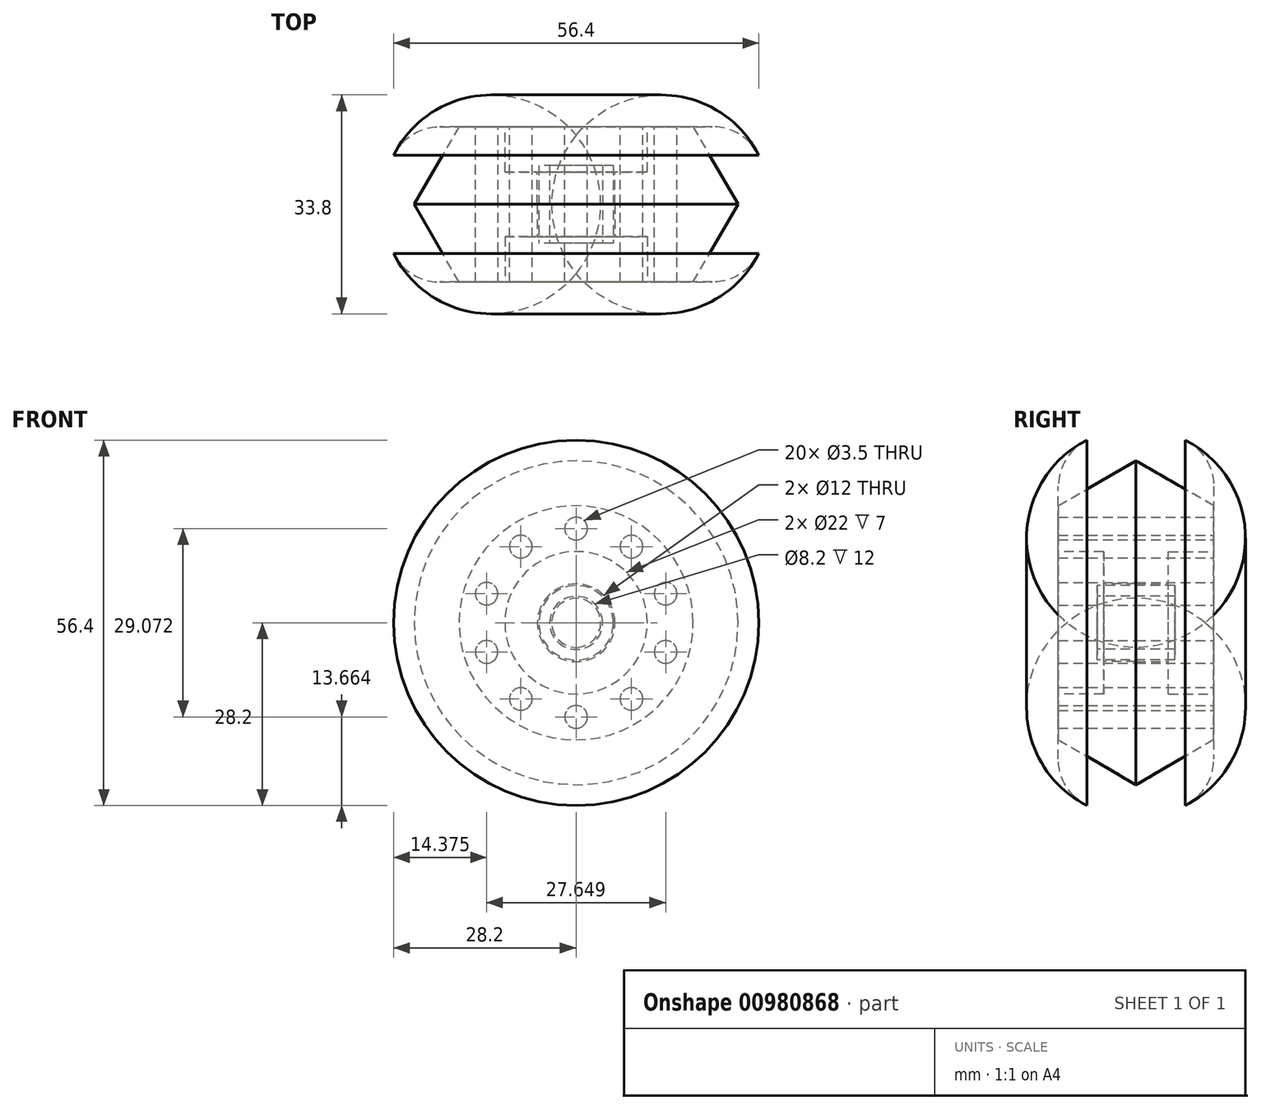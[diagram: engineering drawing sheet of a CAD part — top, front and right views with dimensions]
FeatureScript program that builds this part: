
annotation { "Feature Type Name" : "Feature", "Feature Type Description" : "" }
export const myFeature = defineFeature(function(context is Context, id is Id, definition is map)
    precondition{}
    {
        {
            var Q0;
            Q0=qCreatedBy(makeId("Front.planeOp"),FACE);
            var sketch = newSketch(context, id + "F0", { "sketchPlane" : qUnion([Q0])});
            skCircle(sketch, "E0", {"center": v(0, 0) * mm, "radius": 11 * mm});
            skCircle(sketch, "E1", {"center": v(0, 0) * mm, "radius": 25 * mm});
            skCircle(sketch, "E2", {"center": v(0, 0) * mm, "radius": 6 * mm});
            skCircle(sketch, "E3", {"center": v(0, 0) * mm, "radius": 30 * mm});
            skSolve(sketch);
        }
        {
            var Q0;
            Q0=makeQuery(id+"F0.imprint","IMPRINT",FACE,{"disambiguationData":[TD([[makeQuery(id+"F0.imprint","IMPRINT",EDGE,{"derivedFrom":sQuery(id+"F0.wireOp",EDGE,"E0")}),-1.0]])]});
            var Q1;
            Q1=makeQuery(id+"F0.imprint","IMPRINT",FACE,{"disambiguationData":[TD([[makeQuery(id+"F0.imprint","IMPRINT",EDGE,{"derivedFrom":sQuery(id+"F0.wireOp",EDGE,"E0")}),1.0]])]});
            extrude(context, id + "F1", {"entities" : qUnion([Q0, Q1]), "depth" : 12 * mm, "offsetDistance" : 25 * mm});
        }
        {
            var Q0;
            Q0=makeQuery(id+"F0.imprint","IMPRINT",FACE,{"disambiguationData":[TD([[makeQuery(id+"F0.imprint","IMPRINT",EDGE,{"derivedFrom":sQuery(id+"F0.wireOp",EDGE,"E0")}),1.0]])]});
            extrude(context, id + "F2", {"entities" : qUnion([Q0]), "operationType" : NewBodyOperationType.REMOVE, "depth" : 7 * mm, "offsetDistance" : 25 * mm});
        }
        {
            var Q0;
            Q0=makeQuery(id+"F1.opExtrude","CAP_FACE",FACE,{"disambiguationData":[OSD([sQuery(id+"F0.wireOp",EDGE,"E1"),sQuery(id+"F0.wireOp",EDGE,"E2")])],"isStart":false});
            var sketch = newSketch(context, id + "F3", { "sketchPlane" : qUnion([Q0])});
            skCircle(sketch, "E4", {"center": v(18, 0) * mm, "radius": 2.93 * mm});
            skCircle(sketch, "E5.0", {"center": v(0, 0) * mm, "radius": 11 * mm, "construction": true});
            skCircle(sketch, "E6.0", {"center": v(0, 0) * mm, "radius": 25 * mm, "construction": true});
            skLineSegment(sketch, "E7", {"start": v(11, 0) * mm, "end": v(25, 0) * mm, "construction": true});
            skCircle(sketch, "E8.1.0", {"center": v(0, 18) * mm, "radius": 2.93 * mm});
            skCircle(sketch, "E8.2.0", {"center": v(-18, 0) * mm, "radius": 2.93 * mm});
            skCircle(sketch, "E8.3.0", {"center": v(0, -18) * mm, "radius": 2.93 * mm});
            skLineSegment(sketch, "E9", {"start": v(0, 0) * mm, "end": v(7.78, 7.78) * mm, "construction": true});
            skLineSegment(sketch, "E10", {"start": v(7.78, 7.78) * mm, "end": v(17.68, 17.68) * mm, "construction": true});
            skCircle(sketch, "E11", {"center": v(12.73, 12.73) * mm, "radius": 3.08 * mm});
            skCircle(sketch, "E12.1.0", {"center": v(-12.73, 12.73) * mm, "radius": 3.08 * mm});
            skCircle(sketch, "E12.2.0", {"center": v(-12.73, -12.73) * mm, "radius": 3.08 * mm});
            skCircle(sketch, "E12.3.0", {"center": v(12.73, -12.73) * mm, "radius": 3.08 * mm});
            skSolve(sketch);
        }
        {
            var Q0;
            Q0=qCreatedBy(makeId("Top.planeOp"),FACE);
            var sketch = newSketch(context, id + "F4", { "sketchPlane" : qUnion([Q0])});
            skLineSegment(sketch, "E13", {"start": v(0, 33.2) * mm, "end": v(0, -52.48) * mm, "construction": true});
            skSolve(sketch);
        }
        {
            var Q0;
            Q0=makeQuery(id+"F1.opExtrude","CAP_FACE",FACE,{"disambiguationData":[OSD([sQuery(id+"F0.wireOp",EDGE,"E1"),sQuery(id+"F0.wireOp",EDGE,"E2")])],"isStart":false});
            var sketch = newSketch(context, id + "F5", { "sketchPlane" : qUnion([Q0])});
            skLineSegment(sketch, "E14", {"start": v(-27.1, 0) * mm, "end": v(30.64, 0) * mm});
            skSolve(sketch);
        }
        {
            var Q0;
            Q0=makeQuery(id+"F1.opExtrude","SWEPT_BODY",BODY,{"disambiguationData":[OSD([sQuery(id+"F0.wireOp",EDGE,"E1"),sQuery(id+"F0.wireOp",EDGE,"E2")])]});
            var Q1;
            Q1=sQuery(id+"F5.wireOp",EDGE,"E14");
            transform(context, id + "F6", {"entities" : qUnion([Q0]), "transformType" : TransformType.ROTATION, "transformAxis" : qUnion([Q1]), "angle" : 180 * degree, "makeCopy" : true});
        }
        {
            var Q0;
            Q0=makeQuery(id+"F6.opPattern","COPY",BODY,{"derivedFrom":makeQuery(id+"F1.opExtrude","SWEPT_BODY",BODY,{"disambiguationData":[OSD([sQuery(id+"F0.wireOp",EDGE,"E1"),sQuery(id+"F0.wireOp",EDGE,"E2")])]}),"instanceName":"1"});
            var Q1;
            Q1=sQuery(id+"F4.wireOp",EDGE,"E13");
            transform(context, id + "F7", {"entities" : qUnion([Q0]), "transformType" : TransformType.ROTATION, "transformAxis" : qUnion([Q1]), "angle" : 45 * degree, "makeCopy" : false});
        }
        {
            var Q0;
            Q0=qCreatedBy(makeId("Top.planeOp"),FACE);
            var sketch = newSketch(context, id + "F8", { "sketchPlane" : qUnion([Q0])});
            skLineSegment(sketch, "E15.0", {"start": v(30, 0) * mm, "end": v(-30, 0) * mm, "construction": true});
            skLineSegment(sketch, "E16", {"start": v(-25, -12) * mm, "end": v(-25, 0) * mm, "construction": true});
            skLineSegment(sketch, "E17", {"start": v(-25, -24) * mm, "end": v(-25, -12) * mm, "construction": true});
            skLineSegment(sketch, "E18.0", {"start": v(25, -12) * mm, "end": v(-25, -12) * mm, "construction": true});
            skLineSegment(sketch, "E19", {"start": v(25, 0) * mm, "end": v(25, -12) * mm, "construction": true});
            skLineSegment(sketch, "E20", {"start": v(-25, -12) * mm, "end": v(-18.07, 0) * mm});
            skLineSegment(sketch, "E21.MirrorCS", {"start": v(-25, -12) * mm, "end": v(-18.07, -24) * mm});
            skLineSegment(sketch, "E22", {"start": v(-18.07, 0) * mm, "end": v(-25, 0) * mm});
            skLineSegment(sketch, "E23", {"start": v(-25, -24) * mm, "end": v(-25, 0) * mm});
            skLineSegment(sketch, "E24", {"start": v(-25, -24) * mm, "end": v(-18.07, -24) * mm});
            skSolve(sketch);
        }
        {
            var Q0;
            {var subQ0=sQuery(id+"F8.wireOp",EDGE,"E20");Q0=makeQuery(id+"F8.imprint","IMPRINT",FACE,{"disambiguationData":[TD([[makeQuery(id+"F8.imprint","IMPRINT",EDGE,{"derivedFrom":subQ0}),1.0]])]});}
            var Q1;
            {var subQ0=sQuery(id+"F8.wireOp",EDGE,"E21.MirrorCS");Q1=makeQuery(id+"F8.imprint","IMPRINT",FACE,{"disambiguationData":[TD([[makeQuery(id+"F8.imprint","IMPRINT",EDGE,{"derivedFrom":subQ0}),-1.0]])]});}
            var Q2;
            Q2=sQuery(id+"F4.wireOp",EDGE,"E13");
            revolve(context, id + "F9", {"operationType" : NewBodyOperationType.REMOVE, "surfaceOperationType" : NewSurfaceOperationType.NEW, "entities" : qUnion([Q0, Q1]), "axis" : qUnion([Q2]), "revolveType" : RevolveType.FULL, "oppositeDirection" : true});
        }
        {
            var Q0;
            Q0=qCreatedBy(makeId("Top.planeOp"),FACE);
            var sketch = newSketch(context, id + "F10", { "sketchPlane" : qUnion([Q0])});
            skLineSegment(sketch, "E25.0", {"start": v(30, 0) * mm, "end": v(-30, 0) * mm, "construction": true});
            skLineSegment(sketch, "E26", {"start": v(-25, -12) * mm, "end": v(-18.07, 0) * mm, "construction": true});
            skLineSegment(sketch, "E27.0", {"start": v(-25, -12) * mm, "end": v(-18.07, -24) * mm, "construction": true});
            skLineSegment(sketch, "E28", {"start": v(-30, 0) * mm, "end": v(-30, -12) * mm, "construction": true});
            skPoint(sketch, "E29.0", {"position": v(-25, 0) * mm});
            skPoint(sketch, "E30.0", {"position": v(-25, -24) * mm});
            skLineSegment(sketch, "E31", {"start": v(-18.07, 0) * mm, "end": v(-25, 0) * mm});
            skLineSegment(sketch, "E32", {"start": v(-25, -24) * mm, "end": v(-18.07, -24) * mm});
            skArc(sketch, "E33", {"start": v(-25, 0) * mm, "mid": v(-30, -12) * mm, "end": v(-25, -24) * mm});
            skLineSegment(sketch, "E34", {"start": v(-25, 0) * mm, "end": v(-18.07, 0) * mm});
            skLineSegment(sketch, "E35", {"start": v(-18.07, 0) * mm, "end": v(-25, -12) * mm});
            skLineSegment(sketch, "E36", {"start": v(-25, -12) * mm, "end": v(-18.07, -24) * mm});
            skSolve(sketch);
        }
        {
            var Q0;
            Q0=makeQuery(id+"F10.imprint","IMPRINT",FACE,{"disambiguationData":[TD([[makeQuery(id+"F10.imprint","IMPRINT",EDGE,{"derivedFrom":sQuery(id+"F10.wireOp",EDGE,"E32")}),1.0]])]});
            var Q1;
            Q1=sQuery(id+"F4.wireOp",EDGE,"E13");
            revolve(context, id + "F11", {"surfaceOperationType" : NewSurfaceOperationType.NEW, "entities" : qUnion([Q0]), "axis" : qUnion([Q1]), "revolveType" : RevolveType.FULL});
        }
        {
            var Q0;
            Q0=makeQuery(id+"F1.opExtrude","CAP_FACE",FACE,{"disambiguationData":[OSD([sQuery(id+"F0.wireOp",EDGE,"E1"),sQuery(id+"F0.wireOp",EDGE,"E2")])],"isStart":true});
            var sketch = newSketch(context, id + "F12", { "sketchPlane" : qUnion([Q0])});
            skLineSegment(sketch, "E37", {"start": v(0, -11) * mm, "end": v(0, -18.07) * mm, "construction": true});
            skCircle(sketch, "E38", {"center": v(0, -14.54) * mm, "radius": 1.75 * mm});
            skCircle(sketch, "E39.1.0", {"center": v(8.54, -11.76) * mm, "radius": 1.75 * mm});
            skCircle(sketch, "E39.2.0", {"center": v(13.82, -4.5) * mm, "radius": 1.75 * mm});
            skCircle(sketch, "E39.3.0", {"center": v(13.82, 4.5) * mm, "radius": 1.75 * mm});
            skCircle(sketch, "E39.4.0", {"center": v(8.54, 11.76) * mm, "radius": 1.75 * mm});
            skCircle(sketch, "E39.5.0", {"center": v(0, 14.54) * mm, "radius": 1.75 * mm});
            skCircle(sketch, "E39.6.0", {"center": v(-8.54, 11.76) * mm, "radius": 1.75 * mm});
            skCircle(sketch, "E39.7.0", {"center": v(-13.82, 4.5) * mm, "radius": 1.75 * mm});
            skCircle(sketch, "E39.8.0", {"center": v(-13.82, -4.5) * mm, "radius": 1.75 * mm});
            skCircle(sketch, "E39.9.0", {"center": v(-8.54, -11.76) * mm, "radius": 1.75 * mm});
            skPoint(sketch, "E39.center", {"position": v(0, 0) * mm});
            skSolve(sketch);
        }
        {
            var Q0;
            Q0 = qSketchRegion(id + "F12", true);
            extrude(context, id + "F13", {"entities" : qUnion([Q0]), "operationType" : NewBodyOperationType.REMOVE, "endBound" : BoundingType.THROUGH_ALL, "oppositeDirection" : true, "depth" : 25 * mm, "offsetDistance" : 25 * mm});
        }
        {
            var Q0;
            Q0=makeQuery(id+"F11.opRevolve","SWEPT_EDGE",EDGE,{"disambiguationData":[OSD([sQuery(id+"F10.wireOp",EDGE,"E32"),sQuery(id+"F10.wireOp",EDGE,"E33")])]});
            var Q1;
            Q1=makeQuery(id+"F11.opRevolve","SWEPT_EDGE",EDGE,{"disambiguationData":[OSD([sQuery(id+"F10.wireOp",EDGE,"E33"),sQuery(id+"F10.wireOp",EDGE,"E34")])]});
            fillet(context, id + "F14", {"entities" : qUnion([Q0, Q1]), "radius" : 8 * mm, "tangentPropagation" : true, "allowEdgeOverflow" : false});
        }
        {
            var Q0;
            Q0=makeQuery(id+"F6.opPattern","COPY",FACE,{"derivedFrom":makeQuery(id+"F2.boolean.opBoolean","COPY",FACE,{"derivedFrom":makeQuery(id+"F2.opExtrude","CAP_FACE",FACE,{"disambiguationData":[OSD([sQuery(id+"F0.wireOp",EDGE,"E0"),sQuery(id+"F0.wireOp",EDGE,"E2")])],"isStart":false})}),"instanceName":"1"});
            var sketch = newSketch(context, id + "F15", { "sketchPlane" : qUnion([Q0])});
            skCircle(sketch, "E40", {"center": v(0, 0) * mm, "radius": 4.1 * mm});
            skCircle(sketch, "E41", {"center": v(0, 0) * mm, "radius": 5.75 * mm});
            skSolve(sketch);
        }
        {
            var Q0;
            Q0 = qSketchRegion(id + "F15", true);
            extrude(context, id + "F16", {"entities" : qUnion([Q0]), "oppositeDirection" : true, "depth" : 11 * mm, "offsetDistance" : 25 * mm, "hasSecondDirection" : true, "secondDirectionOppositeDirection" : false, "secondDirectionDepth" : 1 * mm});
        }
    });
